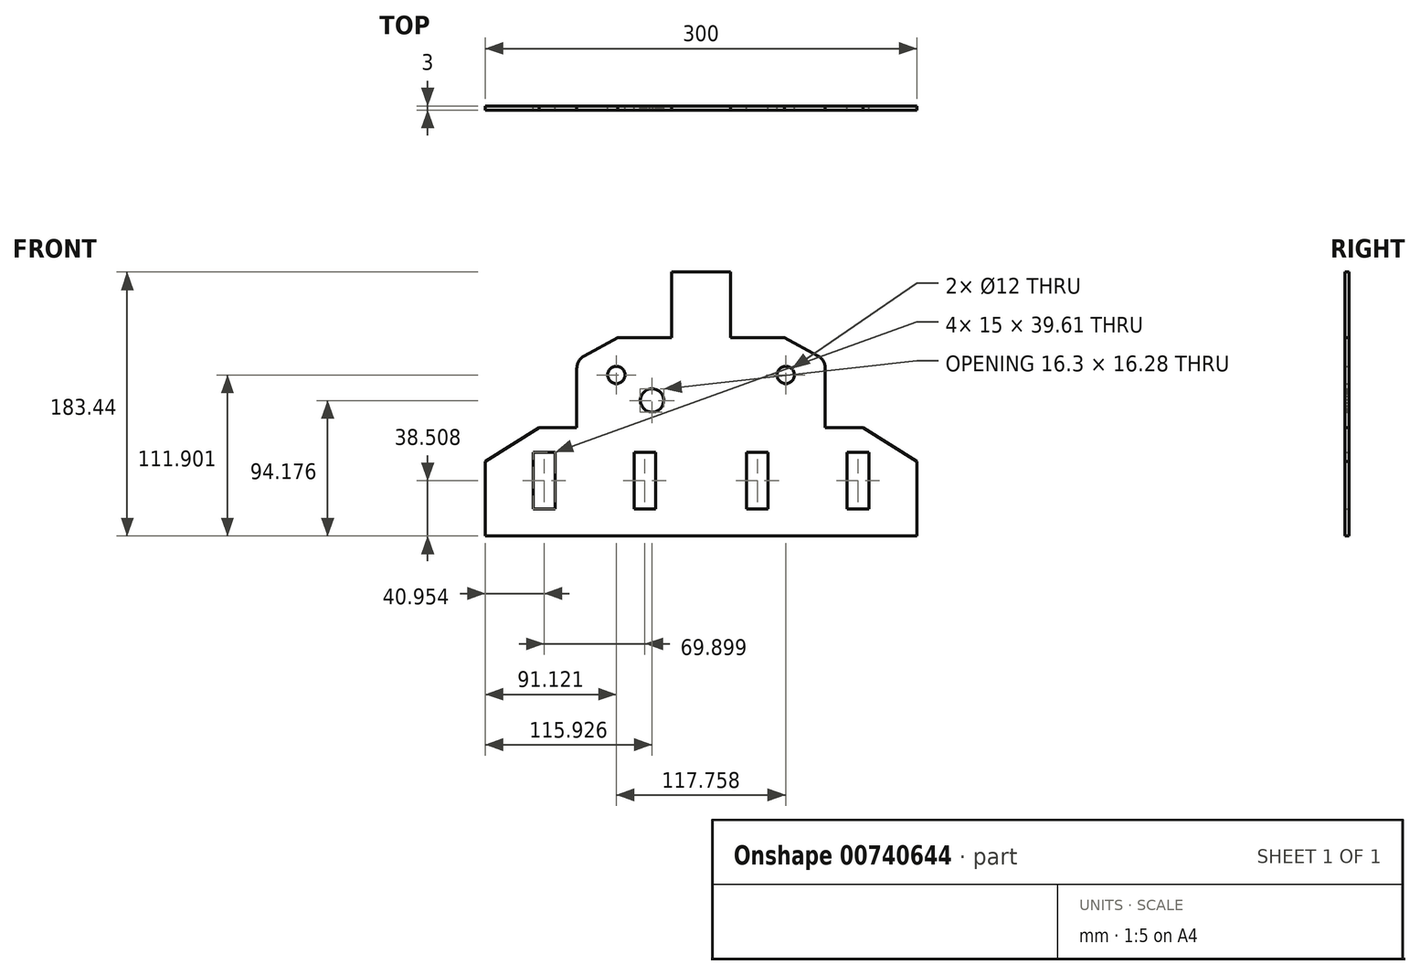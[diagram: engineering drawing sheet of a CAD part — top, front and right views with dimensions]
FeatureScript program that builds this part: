
annotation { "Feature Type Name" : "Feature", "Feature Type Description" : "" }
export const myFeature = defineFeature(function(context is Context, id is Id, definition is map)
    precondition{}
    {
        {
            var Q0;
            Q0=qCreatedBy(makeId("Front.planeOp"),FACE);
            var sketch = newSketch(context, id + "F0", { "sketchPlane" : qUnion([Q0])});
            skLineSegment(sketch, "E0", {"start": v(0, 0) * mm, "end": v(150, 0) * mm, "construction": true});
            skLineSegment(sketch, "E1", {"start": v(0, 0) * mm, "end": v(0, 51.94) * mm});
            skLineSegment(sketch, "E2", {"start": v(0, 51.94) * mm, "end": v(37.39, 75.4) * mm});
            skLineSegment(sketch, "E3", {"start": v(37.39, 75.4) * mm, "end": v(63.65, 75.4) * mm});
            skLineSegment(sketch, "E4", {"start": v(63.65, 75.4) * mm, "end": v(63.65, 116.51) * mm});
            skLineSegment(sketch, "E5", {"start": v(68.86, 125.3) * mm, "end": v(92.06, 137.94) * mm});
            skLineSegment(sketch, "E6", {"start": v(92.06, 137.94) * mm, "end": v(129.58, 137.94) * mm});
            skLineSegment(sketch, "E7", {"start": v(129.58, 137.94) * mm, "end": v(129.58, 183.44) * mm});
            skLineSegment(sketch, "E8", {"start": v(129.58, 183.44) * mm, "end": v(150, 183.44) * mm});
            skCircle(sketch, "E9", {"center": v(91.12, 111.9) * mm, "radius": 6 * mm});
            skLineSegment(sketch, "E10.bottom", {"start": v(33.45, 58.31) * mm, "end": v(48.45, 58.31) * mm});
            skLineSegment(sketch, "E10.top", {"start": v(33.45, 18.7) * mm, "end": v(48.45, 18.7) * mm});
            skLineSegment(sketch, "E10.left", {"start": v(33.45, 58.31) * mm, "end": v(33.45, 18.7) * mm});
            skLineSegment(sketch, "E10.right", {"start": v(48.45, 58.31) * mm, "end": v(48.45, 18.7) * mm});
            skLineSegment(sketch, "E11.bottom", {"start": v(103.35, 58.31) * mm, "end": v(118.35, 58.31) * mm});
            skLineSegment(sketch, "E11.top", {"start": v(103.35, 18.7) * mm, "end": v(118.35, 18.7) * mm});
            skLineSegment(sketch, "E11.left", {"start": v(103.35, 58.31) * mm, "end": v(103.35, 18.7) * mm});
            skLineSegment(sketch, "E11.right", {"start": v(118.35, 58.31) * mm, "end": v(118.35, 18.7) * mm});
            skPoint(sketch, "E12.visualSharp", {"position": v(63.65, 122.45) * mm});
            skArc(sketch, "E12.filletArc", {"start": v(68.86, 125.3) * mm, "mid": v(65.05, 121.62) * mm, "end": v(63.65, 116.51) * mm});
            skLineSegment(sketch, "E13", {"start": v(0, 51.94) * mm, "end": v(0, 0) * mm});
            skLineSegment(sketch, "E14", {"start": v(0, 0) * mm, "end": v(150, 0) * mm});
            skArc(sketch, "E15.MirrorCS", {"start": v(231.14, 125.3) * mm, "mid": v(234.95, 121.62) * mm, "end": v(236.35, 116.51) * mm});
            skLineSegment(sketch, "E16.MirrorCS", {"start": v(266.55, 58.31) * mm, "end": v(251.55, 58.31) * mm});
            skLineSegment(sketch, "E17.MirrorCS", {"start": v(266.55, 18.7) * mm, "end": v(251.55, 18.7) * mm});
            skLineSegment(sketch, "E18.MirrorCS", {"start": v(196.65, 58.31) * mm, "end": v(181.65, 58.31) * mm});
            skLineSegment(sketch, "E19.MirrorCS", {"start": v(300, 0) * mm, "end": v(300, 51.94) * mm});
            skLineSegment(sketch, "E20.MirrorCS", {"start": v(300, 0) * mm, "end": v(150, 0) * mm, "construction": true});
            skLineSegment(sketch, "E21.MirrorCS", {"start": v(170.42, 183.44) * mm, "end": v(150, 183.44) * mm});
            skLineSegment(sketch, "E22.MirrorCS", {"start": v(266.55, 58.31) * mm, "end": v(266.55, 18.7) * mm});
            skCircle(sketch, "E23.MirrorC", {"center": v(208.88, 111.9) * mm, "radius": 6 * mm});
            skLineSegment(sketch, "E24.MirrorCS", {"start": v(196.65, 58.31) * mm, "end": v(196.65, 18.7) * mm});
            skLineSegment(sketch, "E25.MirrorCS", {"start": v(300, 51.94) * mm, "end": v(300, 0) * mm});
            skLineSegment(sketch, "E26.MirrorCS", {"start": v(207.94, 137.94) * mm, "end": v(170.42, 137.94) * mm});
            skPoint(sketch, "E27.MirrorP", {"position": v(236.35, 122.45) * mm});
            skLineSegment(sketch, "E28.MirrorCS", {"start": v(181.65, 58.31) * mm, "end": v(181.65, 18.7) * mm});
            skLineSegment(sketch, "E29.MirrorCS", {"start": v(262.61, 75.4) * mm, "end": v(236.35, 75.4) * mm});
            skLineSegment(sketch, "E30.MirrorCS", {"start": v(236.35, 75.4) * mm, "end": v(236.35, 116.51) * mm});
            skLineSegment(sketch, "E31.MirrorCS", {"start": v(231.14, 125.3) * mm, "end": v(207.94, 137.94) * mm});
            skLineSegment(sketch, "E32.MirrorCS", {"start": v(170.42, 137.94) * mm, "end": v(170.42, 183.44) * mm});
            skLineSegment(sketch, "E33.MirrorCS", {"start": v(196.65, 18.7) * mm, "end": v(181.65, 18.7) * mm});
            skLineSegment(sketch, "E34.MirrorCS", {"start": v(300, 0) * mm, "end": v(150, 0) * mm});
            skLineSegment(sketch, "E35.MirrorCS", {"start": v(300, 51.94) * mm, "end": v(262.61, 75.4) * mm});
            skLineSegment(sketch, "E36.MirrorCS", {"start": v(251.55, 58.31) * mm, "end": v(251.55, 18.7) * mm});
            skCircle(sketch, "E37.cCircle", {"center": v(115.94, 94.2) * mm, "radius": 8.1 * mm, "construction": true});
            skLineSegment(sketch, "E37.0", {"start": v(119.05, 101.75) * mm, "end": v(120.97, 100.63) * mm});
            skLineSegment(sketch, "E37.1", {"start": v(120.97, 100.63) * mm, "end": v(122.52, 99.04) * mm});
            skLineSegment(sketch, "E37.2", {"start": v(122.52, 99.04) * mm, "end": v(123.58, 97.08) * mm});
            skLineSegment(sketch, "E37.3", {"start": v(123.58, 97.08) * mm, "end": v(124.07, 94.9) * mm});
            skLineSegment(sketch, "E37.4", {"start": v(124.07, 94.9) * mm, "end": v(123.96, 92.69) * mm});
            skLineSegment(sketch, "E37.5", {"start": v(123.96, 92.69) * mm, "end": v(123.26, 90.58) * mm});
            skLineSegment(sketch, "E37.6", {"start": v(123.26, 90.58) * mm, "end": v(122, 88.74) * mm});
            skLineSegment(sketch, "E37.7", {"start": v(122, 88.74) * mm, "end": v(120.3, 87.3) * mm});
            skLineSegment(sketch, "E37.8", {"start": v(120.3, 87.3) * mm, "end": v(118.28, 86.38) * mm});
            skLineSegment(sketch, "E37.9", {"start": v(118.28, 86.38) * mm, "end": v(116.09, 86.04) * mm});
            skLineSegment(sketch, "E37.10", {"start": v(116.09, 86.04) * mm, "end": v(113.88, 86.3) * mm});
            skLineSegment(sketch, "E37.11", {"start": v(113.88, 86.3) * mm, "end": v(111.82, 87.15) * mm});
            skLineSegment(sketch, "E37.12", {"start": v(111.82, 87.15) * mm, "end": v(110.07, 88.52) * mm});
            skLineSegment(sketch, "E37.13", {"start": v(110.07, 88.52) * mm, "end": v(108.75, 90.31) * mm});
            skLineSegment(sketch, "E37.14", {"start": v(108.75, 90.31) * mm, "end": v(107.97, 92.4) * mm});
            skLineSegment(sketch, "E37.15", {"start": v(107.97, 92.4) * mm, "end": v(107.78, 94.61) * mm});
            skLineSegment(sketch, "E37.16", {"start": v(107.78, 94.61) * mm, "end": v(108.2, 96.8) * mm});
            skLineSegment(sketch, "E37.17", {"start": v(108.2, 96.8) * mm, "end": v(109.18, 98.8) * mm});
            skLineSegment(sketch, "E37.18", {"start": v(109.18, 98.8) * mm, "end": v(110.67, 100.44) * mm});
            skLineSegment(sketch, "E37.19", {"start": v(110.67, 100.44) * mm, "end": v(112.55, 101.63) * mm});
            skLineSegment(sketch, "E37.20", {"start": v(112.55, 101.63) * mm, "end": v(114.68, 102.27) * mm});
            skLineSegment(sketch, "E37.21", {"start": v(114.68, 102.27) * mm, "end": v(116.9, 102.31) * mm});
            skLineSegment(sketch, "E37.22", {"start": v(116.9, 102.31) * mm, "end": v(119.05, 101.75) * mm});
            skPoint(sketch, "E37.0.midPoint", {"position": v(120.01, 101.2) * mm});
            skSolve(sketch);
        }
        {
            var Q0;
            Q0 = qSketchRegion(id + "F0", true);
            extrude(context, id + "F1", {"entities" : qUnion([Q0]), "depth" : 3 * mm, "offsetDistance" : 25 * mm});
        }
    });
